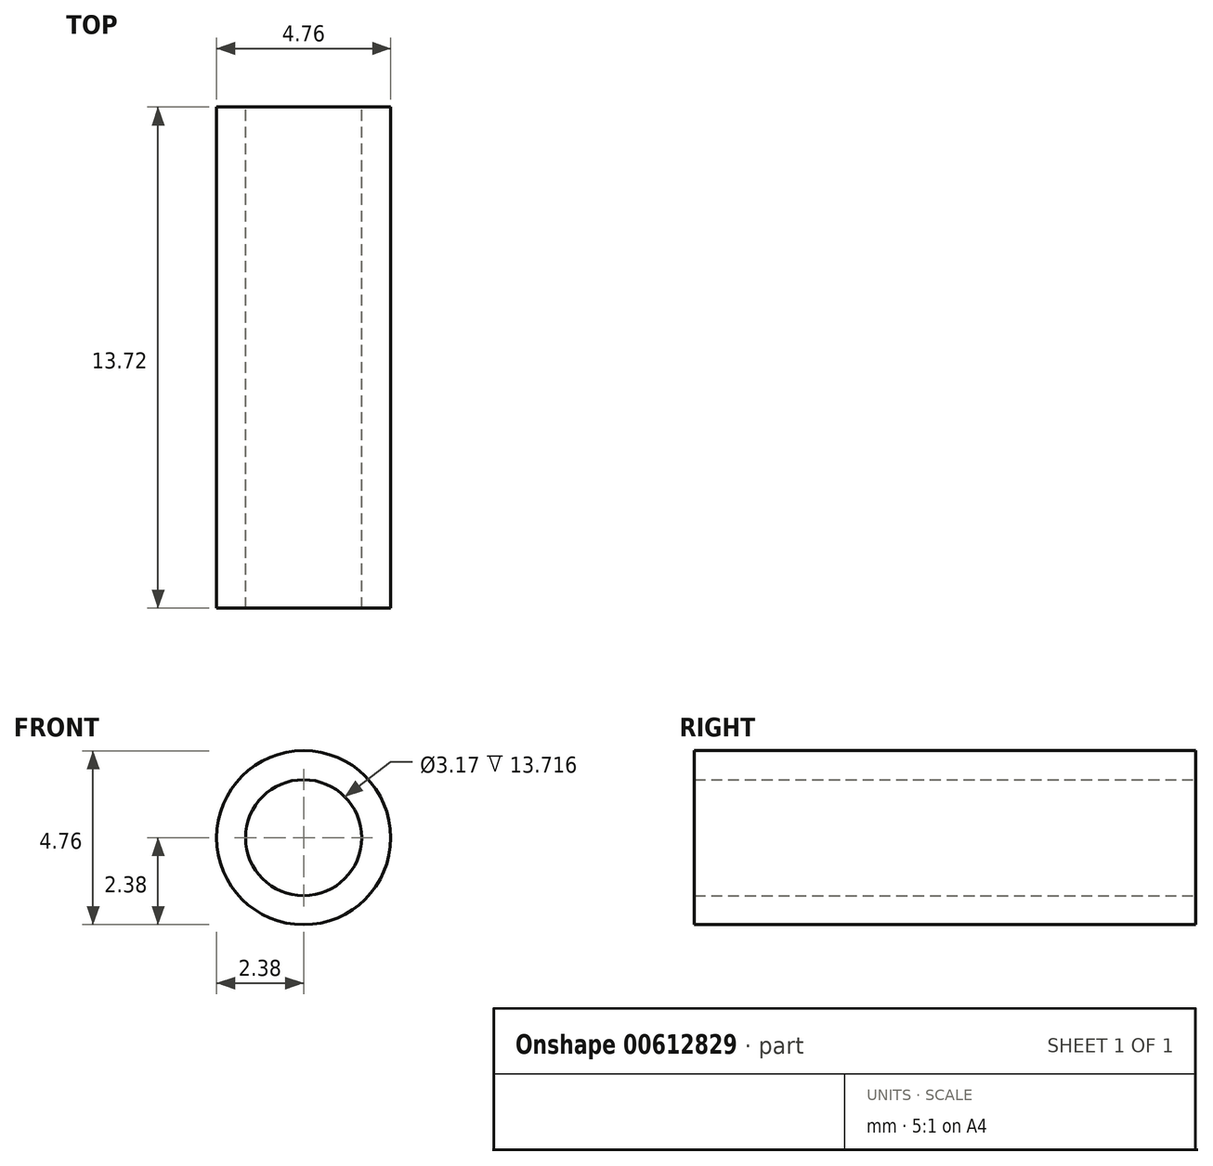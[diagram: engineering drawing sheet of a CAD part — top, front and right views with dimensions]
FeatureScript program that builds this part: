
annotation { "Feature Type Name" : "Feature", "Feature Type Description" : "" }
export const myFeature = defineFeature(function(context is Context, id is Id, definition is map)
    precondition{}
    {
        {
            var Q0;
            Q0=qCreatedBy(makeId("Front.planeOp"),FACE);
            var sketch = newSketch(context, id + "F0", { "sketchPlane" : qUnion([Q0])});
            skCircle(sketch, "E0", {"center": v(0, 0) * mm, "radius": 1.59 * mm});
            skCircle(sketch, "E1", {"center": v(0, 0) * mm, "radius": 2.38 * mm});
            skSolve(sketch);
        }
        {
            var Q0;
            Q0=qSketchRegion(id+"F0",true);
            extrude(context, id + "F1", {"entities" : qUnion([Q0]), "depth" : 13.72 * mm, "symmetric" : true});
        }
    });
